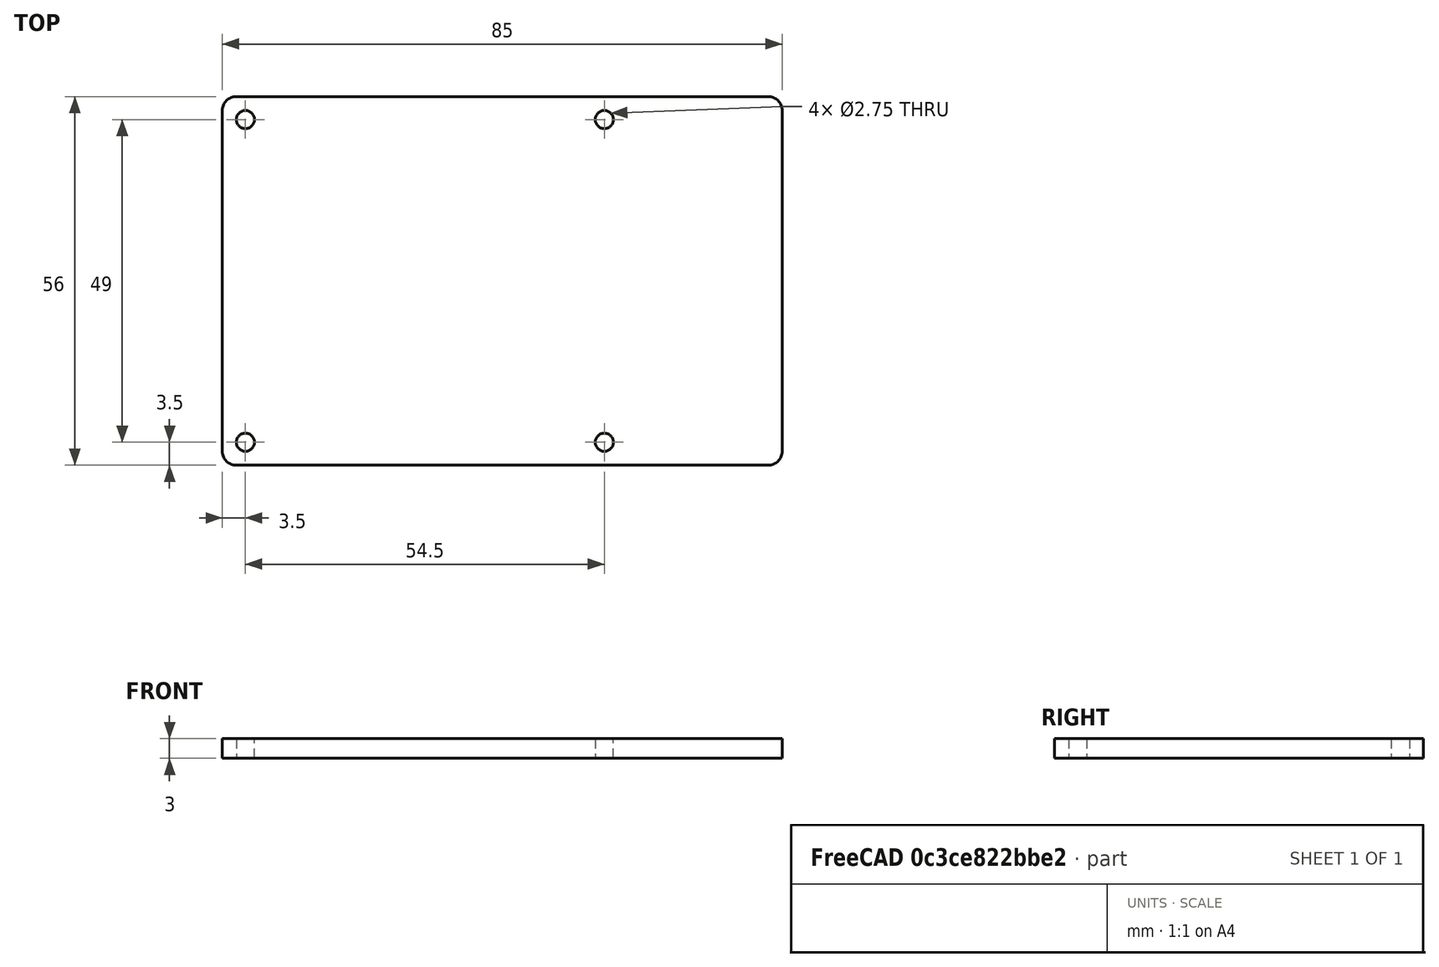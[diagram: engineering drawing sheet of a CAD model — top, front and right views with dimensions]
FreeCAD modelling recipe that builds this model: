
FCSTD DOCUMENT  (FreeCAD 1.0R39285 (Git))
Label: raspberry_pi_3_b
License: All rights reserved
LicenseURL: https://en.wikipedia.org/wiki/All_rights_reserved
objects: Sketcher::SketchObject×1, Spreadsheet::Sheet×1, PartDesign::Pad×1, PartDesign::Body×1
note: 6 computed .brp shape members not serialized (recipe doc carries the construction recipe); baked Part::Feature solids carry a one-line shape summary decoded from their .brp

FEATURE [Sketcher::SketchObject] Sketch  label="RaspberryPiBodySketch"
  ArcFitTolerance = 0
  FullyConstrained = true
  MakeInternals = false
  expr: .Constraints.length = <<dimensions_spreadsheet>>.length
  expr: .Constraints.right_screw_hole_offset_x = <<dimensions_spreadsheet>>.right_screw_hole_offset_x
  expr: .Constraints.screw_hole_diameter = <<dimensions_spreadsheet>>.screw_hole_diameter
  expr: .Constraints.screw_hole_inset = <<dimensions_spreadsheet>>.screw_hole_inset
  expr: .Constraints.width = <<dimensions_spreadsheet>>.width
  expr: Constraints[22] = <<dimensions_spreadsheet>>.corner_radius
  expr: Constraints[24] = <<dimensions_spreadsheet>>.screw_hole_diameter
  expr: Constraints[25] = <<dimensions_spreadsheet>>.screw_hole_diameter
  expr: Constraints[26] = <<dimensions_spreadsheet>>.screw_hole_inset
  expr: Constraints[27] = <<dimensions_spreadsheet>>.screw_hole_diameter
  expr: Constraints[28] = 58 mm
  expr: Constraints[29] = <<dimensions_spreadsheet>>.screw_hole_inset
  expr: Constraints[30] = <<dimensions_spreadsheet>>.screw_hole_inset
  expr: Constraints[32] = <<dimensions_spreadsheet>>.screw_hole_inset
  expr: Constraints[33] = <<dimensions_spreadsheet>>.screw_hole_inset
  sketch-geometry (14):
    g0: ArcOfCircle CenterX=2.12132 CenterY=2.12132 CenterZ=0 NormalX=0 NormalY=0 NormalZ=1 AngleXU=0 Radius=2.12132 StartAngle=3.14159 EndAngle=4.71239
    g1: LineSegment StartX=4e-16 StartY=2.12132 StartZ=0 EndX=4e-16 EndY=53.8787 EndZ=0
    g2: ArcOfCircle CenterX=2.12132 CenterY=53.8787 CenterZ=0 NormalX=0 NormalY=0 NormalZ=1 AngleXU=0 Radius=2.12132 StartAngle=1.5708 EndAngle=3.14159
    g3: LineSegment StartX=2.12132 StartY=56 StartZ=0 EndX=82.8787 EndY=56 EndZ=0
    g4: ArcOfCircle CenterX=82.8787 CenterY=53.8787 CenterZ=0 NormalX=0 NormalY=0 NormalZ=1 AngleXU=0 Radius=2.12132 StartAngle=-1.8e-15 EndAngle=1.5708
    g5: LineSegment StartX=85 StartY=53.8787 StartZ=0 EndX=85 EndY=2.12132 EndZ=0
    g6: ArcOfCircle CenterX=82.8787 CenterY=2.12132 CenterZ=0 NormalX=0 NormalY=0 NormalZ=1 AngleXU=0 Radius=2.12132 StartAngle=4.71239 EndAngle=6.28319
    g7: LineSegment StartX=82.8787 StartY=0 StartZ=0 EndX=2.12132 EndY=0 EndZ=0
    g8: GeomPoint [constr] X=0 Y=0 Z=0
    g9: GeomPoint [constr] X=85 Y=56 Z=0
    g10: Circle CenterX=3.5 CenterY=3.5 CenterZ=0 NormalX=0 NormalY=0 NormalZ=1 AngleXU=0 Radius=1.375
    g11: Circle CenterX=3.5 CenterY=52.5 CenterZ=0 NormalX=0 NormalY=0 NormalZ=1 AngleXU=0 Radius=1.375
    g12: Circle CenterX=58 CenterY=52.5 CenterZ=0 NormalX=0 NormalY=0 NormalZ=1 AngleXU=0 Radius=1.375
    g13: Circle CenterX=58 CenterY=3.5 CenterZ=0 NormalX=0 NormalY=0 NormalZ=1 AngleXU=0 Radius=1.375
  constraints (35):
    c: Tangent(g0,g1) = 1.5708
    c: Tangent(g1,g2) = 1.5708
    c: Tangent(g2,g3) = 1.5708
    c: Tangent(g3,g4) = 1.5708
    c: Tangent(g4,g5) = 1.5708
    c: Tangent(g5,g6) = 1.5708
    c: Tangent(g6,g7) = 1.5708
    c: Tangent(g7,g0) = 1.5708
    c: Horizontal(g3)
    c: Horizontal(g7)
    c: Vertical(g1)
    c: Vertical(g5)
    c: Equal(g0,g2)
    c: Equal(g2,g4)
    c: Equal(g4,g6)
    c: PointOnObject(g8,g1)
    c: PointOnObject(g8,g7)
    c: PointOnObject(g9,g3)
    c: PointOnObject(g9,g5)
    c: Coincident(g8,g-1)
    c: DistanceX(g9) = 85  'length'
    c: DistanceY(g9) = 56  'width'
    c: Distance(g8,g0) = 3
    c: Diameter(g10) = 2.75  'screw_hole_diameter'
    c: Diameter(g11) = 2.75
    c: Diameter(g12) = 2.75
    c: DistanceY(g12,g3) = 3.5
    c: Diameter(g13) = 2.75
    c: DistanceX(g12) = 58
    c: DistanceX(g11) = 3.5
    c: DistanceY(g11,g2) = 3.5
    c: DistanceX(g13) = 58  'right_screw_hole_offset_x'
    c: DistanceY(g13) = 3.5
    c: DistanceX(g10) = 3.5
    c: DistanceY(g10) = 3.5  'screw_hole_inset'
FEATURE [Spreadsheet::Sheet] Spreadsheet  label="dimensions_spreadsheet"
  cells = A1='Name; B1='Description; C1='Value; A2='width; B2='Length in the Y direction; C2(width)=56; A3='length; B3='Length in the X direction; C3(length)=85; A4='screw_hole_inset; B4='Distance from edge to center of screw hole; C4(screw_hole_inset)=3.5; A5='right_screw_hole_offset_x; B5='Distance from Y axis to center of right screw holes; C5(right_screw_hole_offset_x)=58; A6='screw_hole_grounding_diameter; B6='Diameter of screw hole grounding material; C6(screw_hole_grounding_diameter)=6; A7='screw_hole_diameter; B7='Diameter of screw hole; C7(screw_hole_diameter)=2.75; A8='corner_radius; B8='Radius of each corner of the PCB; C8(corner_radius)=3
FEATURE [PartDesign::Pad] Pad  label="RaspberryPiBodyPad"
  Direction = (0,0,1)
  Length = 3
  Length2 = 10
  Profile = -> Sketch
  ReferenceAxis = -> Sketch [N_Axis]
  Refine = true
  Suppressed = false
  Type = 0
FEATURE [PartDesign::Body] Body
  AllowCompound = false
  Group = -> [Sketch,Pad]
  Origin = -> Origin
  Tip = -> Pad
